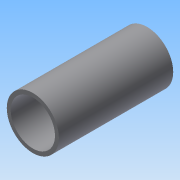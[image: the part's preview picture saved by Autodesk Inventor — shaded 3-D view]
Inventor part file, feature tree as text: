
AUTODESK INVENTOR PART (.ipt)
format: ipt  version: 2015 SP1 (Build 190203100, 203)  size: 79,872 bytes
history: native  units: mm
features: extrude x1, sketch x1
ambient origin geometry x8: Origin, YZ Plane, XZ Plane, XY Plane, X Axis, Y Axis, Z Axis, Center Point
bodies: Solid1 (feature_tree)
feature tree (2):
  extrude  "Extrusion1"  Depth=77.978mm
  sketch  "Sketch1"  dims[d0=30.226mm d1=35.56mm d2=77.978mm d3=0.0mm]
